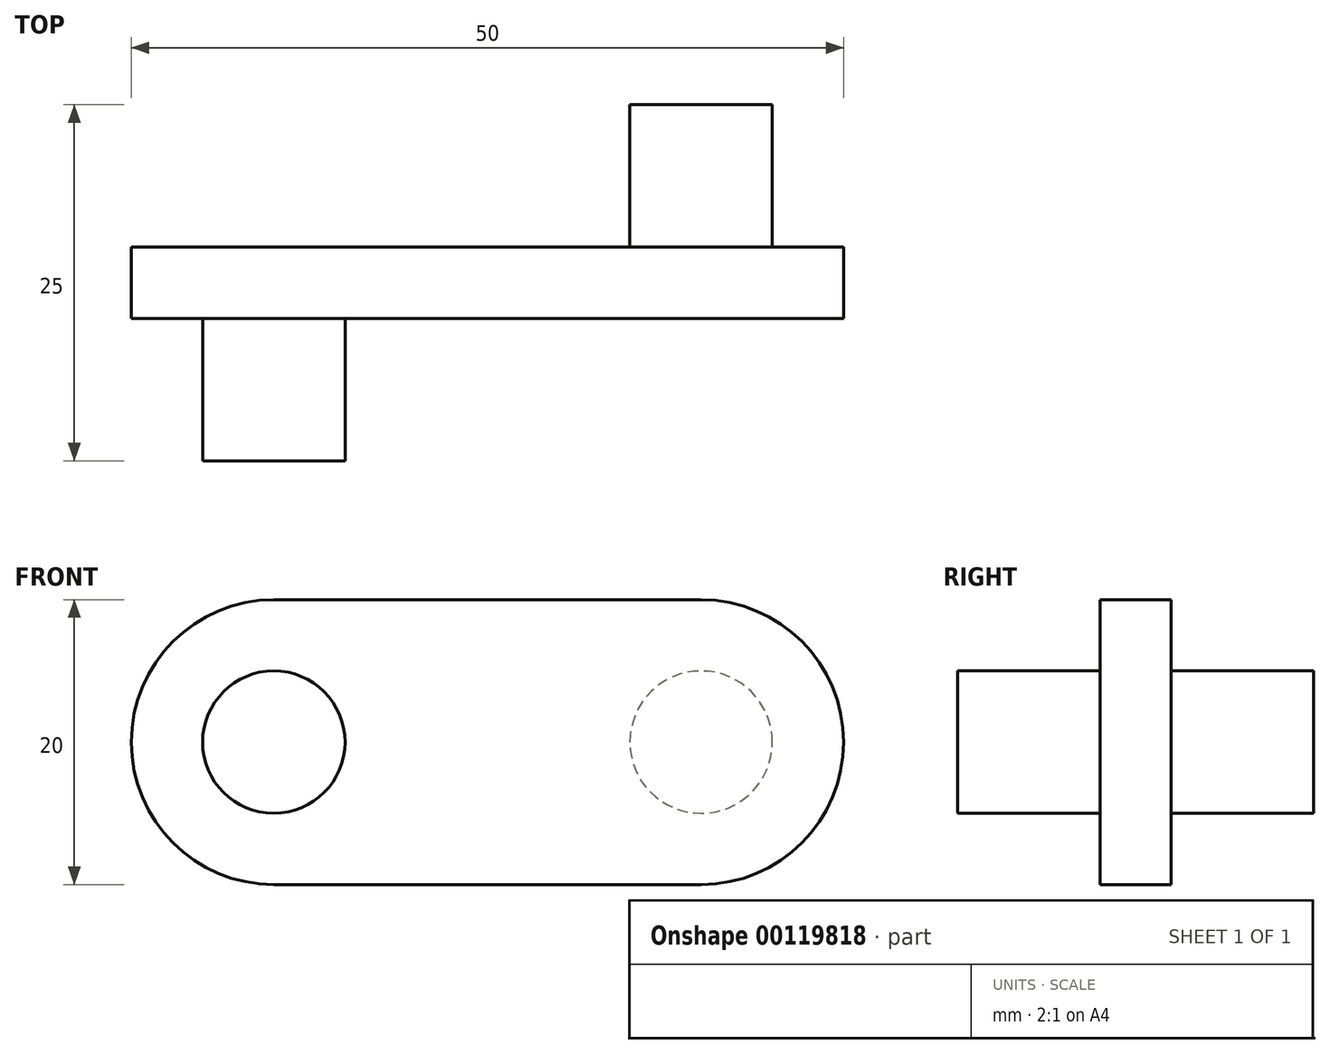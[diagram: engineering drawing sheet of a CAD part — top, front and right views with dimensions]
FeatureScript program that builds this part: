
annotation { "Feature Type Name" : "Feature", "Feature Type Description" : "" }
export const myFeature = defineFeature(function(context is Context, id is Id, definition is map)
    precondition{}
    {
        {
            var Q0;
            Q0=qCreatedBy(makeId("Front.planeOp"),FACE);
            var sketch = newSketch(context, id + "F0", { "sketchPlane" : qUnion([Q0])});
            skLineSegment(sketch, "E0", {"start": v(0, 0) * mm, "end": v(30, 0) * mm});
            skLineSegment(sketch, "E1", {"start": v(0, 20) * mm, "end": v(30, 20) * mm});
            skArc(sketch, "E2", {"start": v(0, 20) * mm, "mid": v(-10, 10) * mm, "end": v(0, 0) * mm});
            skArc(sketch, "E3", {"start": v(30, 0) * mm, "mid": v(40, 10) * mm, "end": v(30, 20) * mm});
            skLineSegment(sketch, "E4", {"start": v(-15.31, 10) * mm, "end": v(68.55, 10) * mm, "construction": true});
            skSolve(sketch);
        }
        {
            var Q0;
            Q0 = qSketchRegion(id + "F0", true);
            extrude(context, id + "F1", {"entities" : qUnion([Q0]), "depth" : 5 * mm});
        }
        {
            var Q0;
            Q0=makeQuery(id+"F1.opExtrude","CAP_FACE",FACE,{"disambiguationData":[OSD([sQuery(id+"F0.wireOp",EDGE,"E0"),sQuery(id+"F0.wireOp",EDGE,"E1"),sQuery(id+"F0.wireOp",EDGE,"E2"),sQuery(id+"F0.wireOp",EDGE,"E3")])],"isStart":false});
            var sketch = newSketch(context, id + "F2", { "sketchPlane" : qUnion([Q0])});
            skCircle(sketch, "E5", {"center": v(0, 10) * mm, "radius": 5 * mm});
            skSolve(sketch);
        }
        {
            var Q0;
            Q0 = qSketchRegion(id + "F2", true);
            extrude(context, id + "F3", {"entities" : qUnion([Q0]), "operationType" : NewBodyOperationType.ADD, "depth" : 10 * mm});
        }
        {
            var Q0;
            Q0=makeQuery(id+"F0.imprint","IMPRINT",FACE,{"disambiguationData":[TD([[makeQuery(id+"F0.imprint","IMPRINT",EDGE,{"derivedFrom":sQuery(id+"F0.wireOp",EDGE,"E0")}),1.0]])]});
            var sketch = newSketch(context, id + "F4", { "sketchPlane" : qUnion([Q0])});
            skCircle(sketch, "E6", {"center": v(30, 10) * mm, "radius": 5 * mm});
            skSolve(sketch);
        }
        {
            var Q0;
            Q0 = qSketchRegion(id + "F4", true);
            extrude(context, id + "F5", {"entities" : qUnion([Q0]), "operationType" : NewBodyOperationType.ADD, "oppositeDirection" : true, "depth" : 10 * mm});
        }
    });
